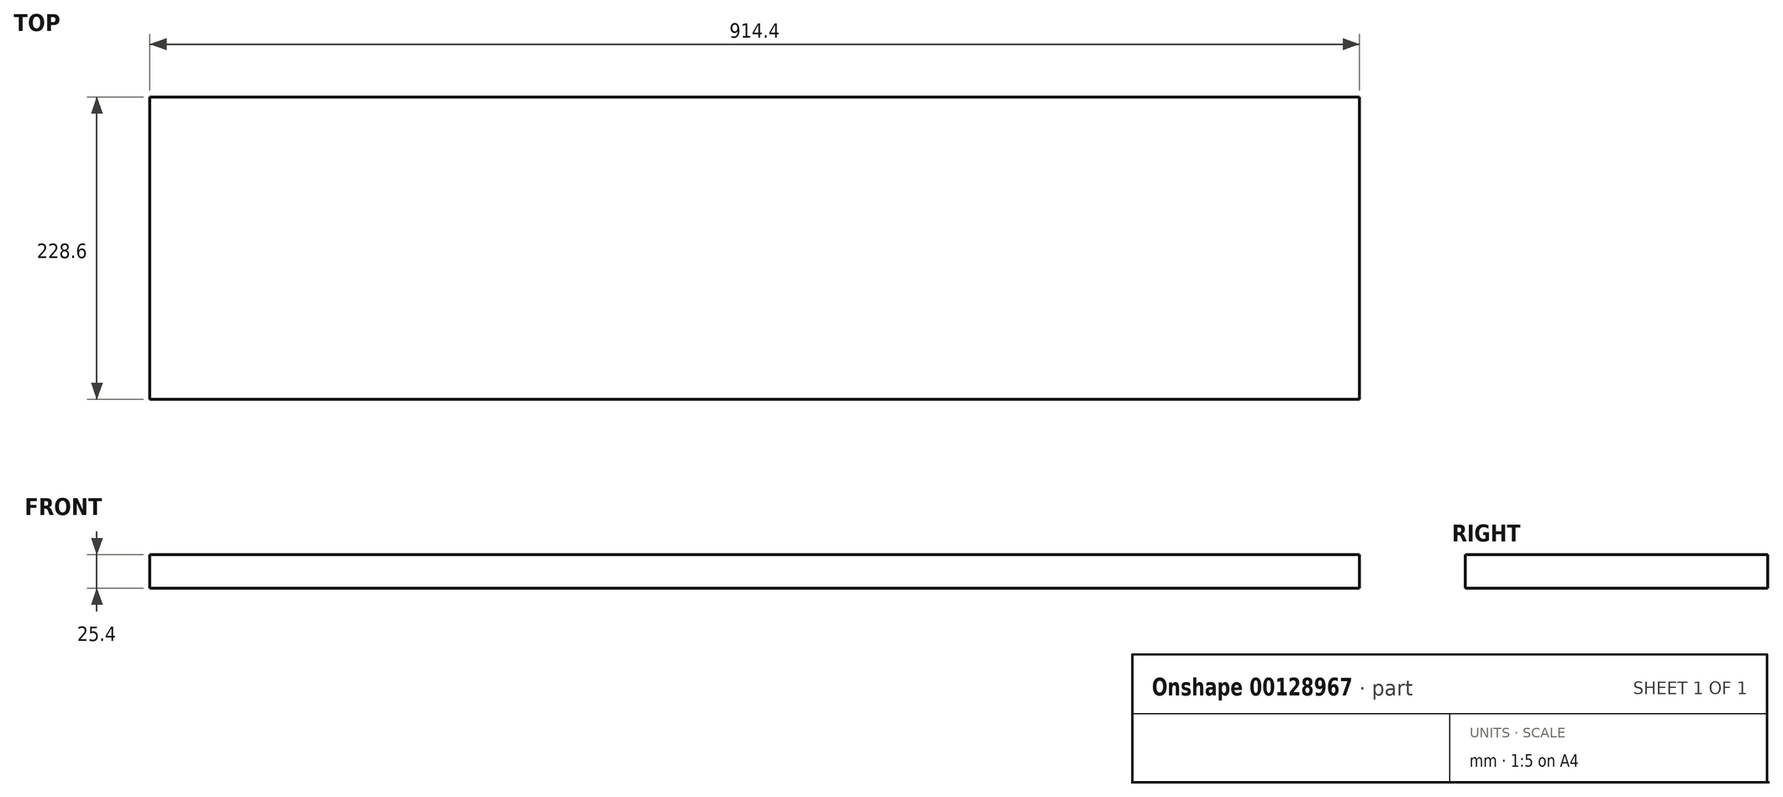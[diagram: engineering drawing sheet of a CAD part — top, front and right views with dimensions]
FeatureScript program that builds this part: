
annotation { "Feature Type Name" : "Feature", "Feature Type Description" : "" }
export const myFeature = defineFeature(function(context is Context, id is Id, definition is map)
    precondition{}
    {
        {
            var Q0;
            Q0=qCreatedBy(makeId("Top.planeOp"),FACE);
            var sketch = newSketch(context, id + "F0", { "sketchPlane" : qUnion([Q0])});
            skLineSegment(sketch, "E0.bottom", {"start": v(0, 0) * mm, "end": v(-914.4, 0) * mm});
            skLineSegment(sketch, "E0.top", {"start": v(0, 228.6) * mm, "end": v(-914.4, 228.6) * mm});
            skLineSegment(sketch, "E0.left", {"start": v(0, 0) * mm, "end": v(0, 228.6) * mm});
            skLineSegment(sketch, "E0.right", {"start": v(-914.4, 0) * mm, "end": v(-914.4, 228.6) * mm});
            skSolve(sketch);
        }
        {
            var Q0;
            Q0=qSketchRegion(id+"F0",true);
            extrude(context, id + "F1", {"entities" : qUnion([Q0]), "depth" : 25.4 * mm});
        }
    });
